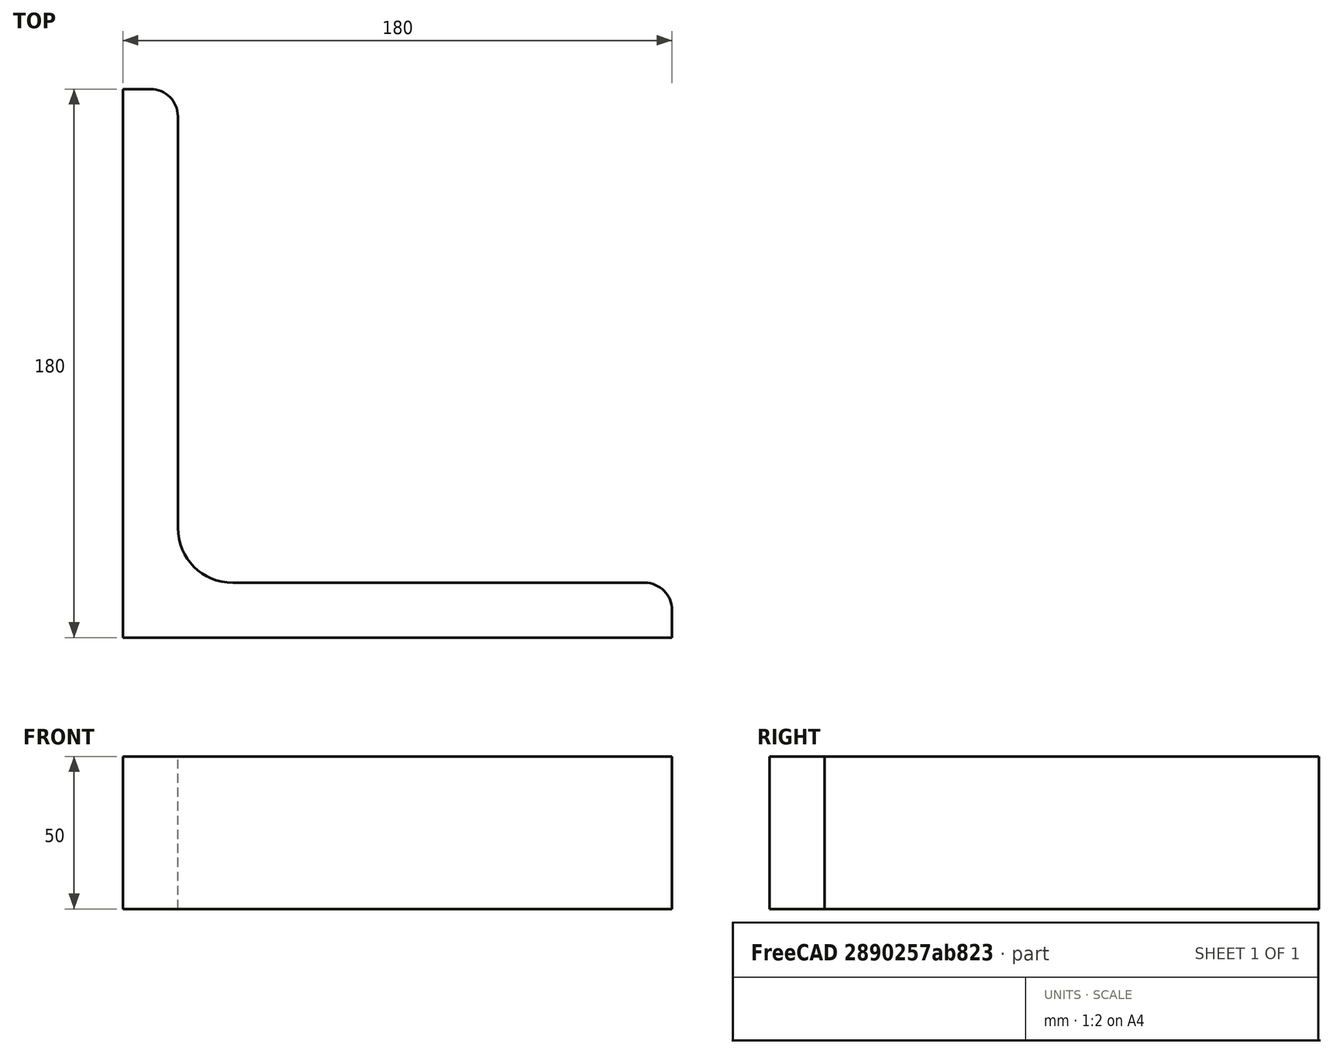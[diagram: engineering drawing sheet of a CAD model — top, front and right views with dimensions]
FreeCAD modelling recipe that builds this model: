
FCSTD DOCUMENT  (FreeCAD 0.15R4671 (Git))
Label: Angle Bar L180x180x18 EN10056 S235JR
License: All rights reserved
LicenseURL: http://en.wikipedia.org/wiki/All_rights_reserved
objects: Sketcher::SketchObject×1, Part::Extrusion×1
note: 2 computed .brp shape members not serialized (recipe doc carries the construction recipe); baked Part::Feature solids carry a one-line shape summary decoded from their .brp

FEATURE [Sketcher::SketchObject] Sketch
  sketch-geometry (9):
    g0: LineSegment StartX=0 StartY=0 StartZ=0 EndX=180 EndY=0 EndZ=0
    g1: LineSegment StartX=180 StartY=0 StartZ=0 EndX=180 EndY=9 EndZ=0
    g2: LineSegment StartX=171 StartY=18 StartZ=0 EndX=36 EndY=18 EndZ=0
    g3: LineSegment StartX=0 StartY=0 StartZ=0 EndX=0 EndY=180 EndZ=0
    g4: LineSegment StartX=0 StartY=180 StartZ=0 EndX=9 EndY=180 EndZ=0
    g5: LineSegment StartX=18 StartY=171 StartZ=0 EndX=18 EndY=36 EndZ=0
    g6: ArcOfCircle CenterX=36 CenterY=36 CenterZ=0 NormalX=0 NormalY=0 NormalZ=1 Radius=18 StartAngle=3.14159 EndAngle=4.71239
    g7: ArcOfCircle CenterX=9 CenterY=171 CenterZ=0 NormalX=0 NormalY=0 NormalZ=1 Radius=9 StartAngle=0 EndAngle=1.5708
    g8: ArcOfCircle CenterX=171 CenterY=9 CenterZ=0 NormalX=0 NormalY=0 NormalZ=1 Radius=9 StartAngle=0 EndAngle=1.5708
  constraints (23):
    c: Coincident(g0,g-1)
    c: Horizontal(g0)
    c: Coincident(g1,g0)
    c: Vertical(g1)
    c: Horizontal(g2)
    c: Coincident(g3,g-1)
    c: Vertical(g3)
    c: Coincident(g4,g3)
    c: Horizontal(g4)
    c: Vertical(g5)
    c: Tangent(g5,g6) = -1.5708
    c: Tangent(g2,g6) = 1.5708
    c: Tangent(g4,g7) = 1.5708
    c: Tangent(g5,g7) = 1.5708
    c: Tangent(g2,g8) = -1.5708
    c: Tangent(g1,g8) = -1.5708
    c: DistanceX(g0) = 180
    c: DistanceY(g3) = 180
    c: DistanceY(g0,g2) = 18
    c: DistanceX(g3,g5) = 18
    c: Radius(g6) = 18
    c: Radius(g8) = 9
    c: Radius(g7) = 9
FEATURE [Part::Extrusion] Extrude  label="Angle Bar L180x180x18 EN10056 S235JR"
  Base = -> Sketch
  Dir = (0,0,50)
  Solid = true
